# Revit family: DPL_Surface
name_source: partatom
category: Lighting Fixtures
revit_build: Autodesk Revit 2014 (Build: 20130308_1515(x64)
units: mm (PartAtom-declared; Revit-internal decimal feet)

## types (1)
- DL_DPL
    Apparent Load = 4 VA
    Application Note = Install photoluminescent exit signs only in locations
where an external illumination source is present, is deemed reliable, and
is supplied by a circuit not controlled by automatic timers or sensors, and
where controls are accessible only to authorized personnel. A minimum
of 5 foot-candle(54lux) external illumination of unfiltered metal halide,
fluorescent, mercury vapor or LED charging light sources required on
sign face at all times of building occupancy.
    Certification = UL 924 Listed
NFPA 101 Life Safety Code
CEC T20 Compliant
    Default Elevation = 48.000"
    Description = The DPL Series of photoluminescent exit signage offers exit compliance with UL listed legible viewing distances of 50', 75' and 100'. The DPL photoluminescent exit signs do not require AC or electrical power. ALl signs have a 25 year lifecycle.
    EXIT - Single Face = Yes
    End = C : C1
    Features = Available in Aluminum Frame, ABS Thermoplastic, Poly-Metal or Acrylic Construction
Maintenance Free Exit Compliance
No Electricity Required
Quick Installation
Made in USA
Wall, Ceiling or End Mount
UL924 Listed
    Finish = Paint - Hubbell - Light Silver
    Glass = Hubbell - Yellow-Glass
    Holder Material = Hubbell - Steel
    Lamp = LED Lamp
    Lens = Hubbell - Green Glass
    Load Classification = Lighting
    Manufacturer = DUAL-LITE
    Model = DPL
    Product Documentation Link = https://hubbellcdn.com
    Product Page URL = https://www.hubbell.com
    Type Comments = Exit Light
    URL = https://www.hubbell.com
    Wall Plate Material = Hubbell - Steel
    Warranty = 5 Year Full
    Wattage Comments = 3.72 W
    Watts = 4 W

## geometry (parser evidence)
native form markers: Blend x2, Sweep x4
no freeform markers — native parametric forms only
